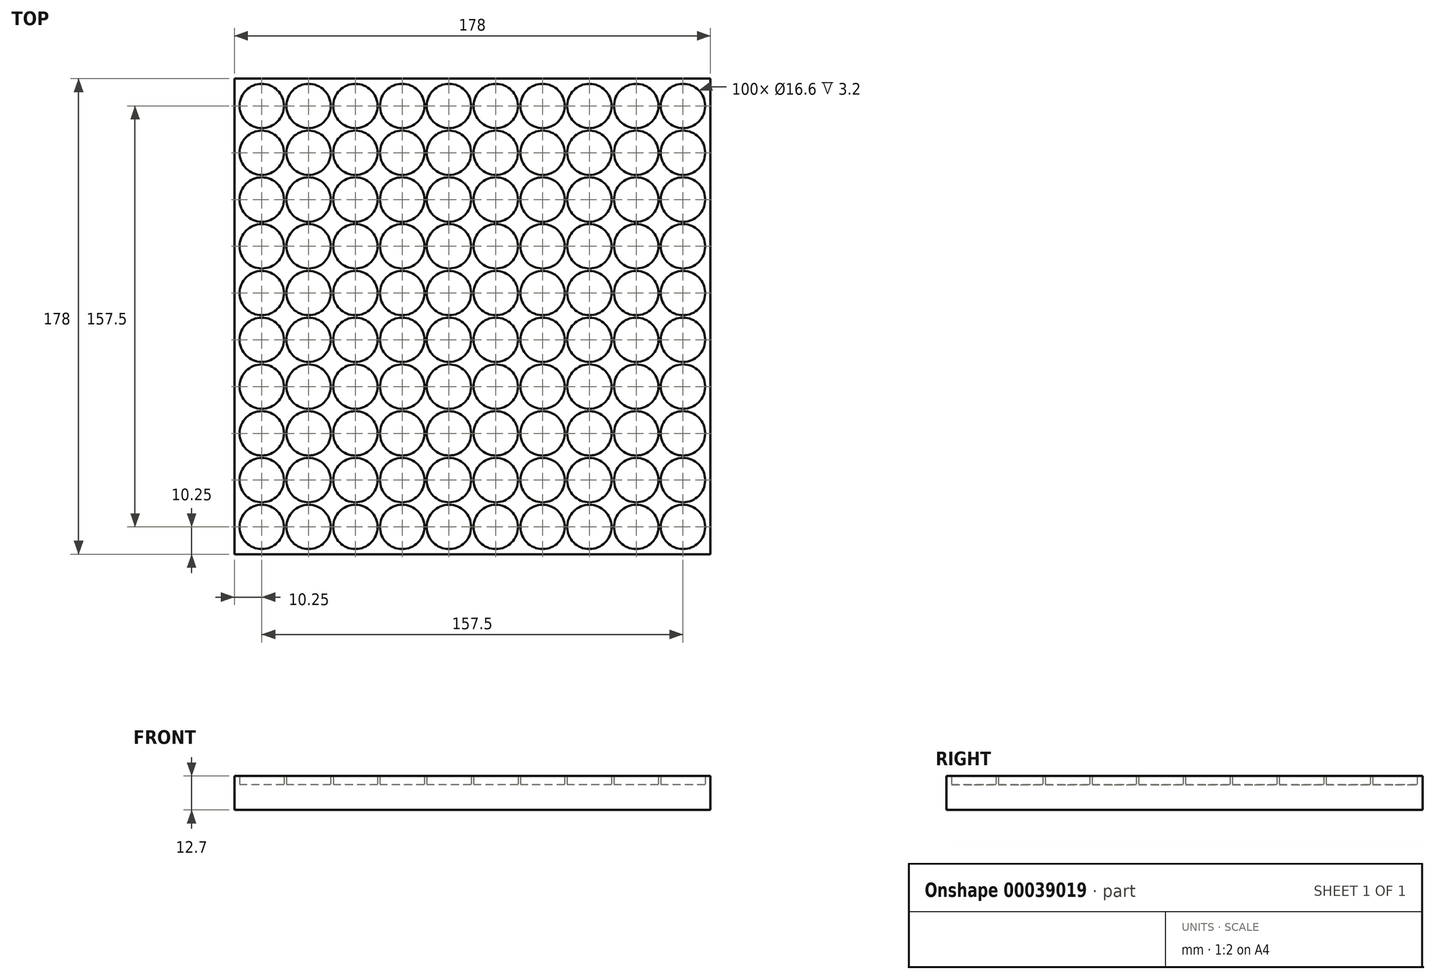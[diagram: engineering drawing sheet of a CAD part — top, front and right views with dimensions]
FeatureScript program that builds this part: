
annotation { "Feature Type Name" : "Feature", "Feature Type Description" : "" }
export const myFeature = defineFeature(function(context is Context, id is Id, definition is map)
    precondition{}
    {
        {
            var Q0;
            Q0=qCreatedBy(makeId("Top.planeOp"),FACE);
            var sketch = newSketch(context, id + "F0", { "sketchPlane" : qUnion([Q0])});
            skCircle(sketch, "E0", {"center": v(0, 0) * mm, "radius": 8.3 * mm});
            skCircle(sketch, "E1.0.1.0", {"center": v(0, 17.5) * mm, "radius": 8.3 * mm});
            skCircle(sketch, "E1.0.2.0", {"center": v(0, 35) * mm, "radius": 8.3 * mm});
            skCircle(sketch, "E1.0.3.0", {"center": v(0, 52.5) * mm, "radius": 8.3 * mm});
            skCircle(sketch, "E1.0.4.0", {"center": v(0, 70) * mm, "radius": 8.3 * mm});
            skCircle(sketch, "E1.0.5.0", {"center": v(0, 87.5) * mm, "radius": 8.3 * mm});
            skCircle(sketch, "E1.0.6.0", {"center": v(0, 105) * mm, "radius": 8.3 * mm});
            skCircle(sketch, "E1.0.7.0", {"center": v(0, 122.5) * mm, "radius": 8.3 * mm});
            skCircle(sketch, "E1.0.8.0", {"center": v(0, 140) * mm, "radius": 8.3 * mm});
            skCircle(sketch, "E1.0.9.0", {"center": v(0, 157.5) * mm, "radius": 8.3 * mm});
            skCircle(sketch, "E1.1.0.0", {"center": v(17.5, 0) * mm, "radius": 8.3 * mm});
            skCircle(sketch, "E1.1.1.0", {"center": v(17.5, 17.5) * mm, "radius": 8.3 * mm});
            skCircle(sketch, "E1.1.2.0", {"center": v(17.5, 35) * mm, "radius": 8.3 * mm});
            skCircle(sketch, "E1.1.3.0", {"center": v(17.5, 52.5) * mm, "radius": 8.3 * mm});
            skCircle(sketch, "E1.1.4.0", {"center": v(17.5, 70) * mm, "radius": 8.3 * mm});
            skCircle(sketch, "E1.1.5.0", {"center": v(17.5, 87.5) * mm, "radius": 8.3 * mm});
            skCircle(sketch, "E1.1.6.0", {"center": v(17.5, 105) * mm, "radius": 8.3 * mm});
            skCircle(sketch, "E1.1.7.0", {"center": v(17.5, 122.5) * mm, "radius": 8.3 * mm});
            skCircle(sketch, "E1.1.8.0", {"center": v(17.5, 140) * mm, "radius": 8.3 * mm});
            skCircle(sketch, "E1.1.9.0", {"center": v(17.5, 157.5) * mm, "radius": 8.3 * mm});
            skCircle(sketch, "E1.2.0.0", {"center": v(35, 0) * mm, "radius": 8.3 * mm});
            skCircle(sketch, "E1.2.1.0", {"center": v(35, 17.5) * mm, "radius": 8.3 * mm});
            skCircle(sketch, "E1.2.2.0", {"center": v(35, 35) * mm, "radius": 8.3 * mm});
            skCircle(sketch, "E1.2.3.0", {"center": v(35, 52.5) * mm, "radius": 8.3 * mm});
            skCircle(sketch, "E1.2.4.0", {"center": v(35, 70) * mm, "radius": 8.3 * mm});
            skCircle(sketch, "E1.2.5.0", {"center": v(35, 87.5) * mm, "radius": 8.3 * mm});
            skCircle(sketch, "E1.2.6.0", {"center": v(35, 105) * mm, "radius": 8.3 * mm});
            skCircle(sketch, "E1.2.7.0", {"center": v(35, 122.5) * mm, "radius": 8.3 * mm});
            skCircle(sketch, "E1.2.8.0", {"center": v(35, 140) * mm, "radius": 8.3 * mm});
            skCircle(sketch, "E1.2.9.0", {"center": v(35, 157.5) * mm, "radius": 8.3 * mm});
            skCircle(sketch, "E1.3.0.0", {"center": v(52.5, 0) * mm, "radius": 8.3 * mm});
            skCircle(sketch, "E1.3.1.0", {"center": v(52.5, 17.5) * mm, "radius": 8.3 * mm});
            skCircle(sketch, "E1.3.2.0", {"center": v(52.5, 35) * mm, "radius": 8.3 * mm});
            skCircle(sketch, "E1.3.3.0", {"center": v(52.5, 52.5) * mm, "radius": 8.3 * mm});
            skCircle(sketch, "E1.3.4.0", {"center": v(52.5, 70) * mm, "radius": 8.3 * mm});
            skCircle(sketch, "E1.3.5.0", {"center": v(52.5, 87.5) * mm, "radius": 8.3 * mm});
            skCircle(sketch, "E1.3.6.0", {"center": v(52.5, 105) * mm, "radius": 8.3 * mm});
            skCircle(sketch, "E1.3.7.0", {"center": v(52.5, 122.5) * mm, "radius": 8.3 * mm});
            skCircle(sketch, "E1.3.8.0", {"center": v(52.5, 140) * mm, "radius": 8.3 * mm});
            skCircle(sketch, "E1.3.9.0", {"center": v(52.5, 157.5) * mm, "radius": 8.3 * mm});
            skCircle(sketch, "E1.4.0.0", {"center": v(70, 0) * mm, "radius": 8.3 * mm});
            skCircle(sketch, "E1.4.1.0", {"center": v(70, 17.5) * mm, "radius": 8.3 * mm});
            skCircle(sketch, "E1.4.2.0", {"center": v(70, 35) * mm, "radius": 8.3 * mm});
            skCircle(sketch, "E1.4.3.0", {"center": v(70, 52.5) * mm, "radius": 8.3 * mm});
            skCircle(sketch, "E1.4.4.0", {"center": v(70, 70) * mm, "radius": 8.3 * mm});
            skCircle(sketch, "E1.4.5.0", {"center": v(70, 87.5) * mm, "radius": 8.3 * mm});
            skCircle(sketch, "E1.4.6.0", {"center": v(70, 105) * mm, "radius": 8.3 * mm});
            skCircle(sketch, "E1.4.7.0", {"center": v(70, 122.5) * mm, "radius": 8.3 * mm});
            skCircle(sketch, "E1.4.8.0", {"center": v(70, 140) * mm, "radius": 8.3 * mm});
            skCircle(sketch, "E1.4.9.0", {"center": v(70, 157.5) * mm, "radius": 8.3 * mm});
            skCircle(sketch, "E1.5.0.0", {"center": v(87.5, 0) * mm, "radius": 8.3 * mm});
            skCircle(sketch, "E1.5.1.0", {"center": v(87.5, 17.5) * mm, "radius": 8.3 * mm});
            skCircle(sketch, "E1.5.2.0", {"center": v(87.5, 35) * mm, "radius": 8.3 * mm});
            skCircle(sketch, "E1.5.3.0", {"center": v(87.5, 52.5) * mm, "radius": 8.3 * mm});
            skCircle(sketch, "E1.5.4.0", {"center": v(87.5, 70) * mm, "radius": 8.3 * mm});
            skCircle(sketch, "E1.5.5.0", {"center": v(87.5, 87.5) * mm, "radius": 8.3 * mm});
            skCircle(sketch, "E1.5.6.0", {"center": v(87.5, 105) * mm, "radius": 8.3 * mm});
            skCircle(sketch, "E1.5.7.0", {"center": v(87.5, 122.5) * mm, "radius": 8.3 * mm});
            skCircle(sketch, "E1.5.8.0", {"center": v(87.5, 140) * mm, "radius": 8.3 * mm});
            skCircle(sketch, "E1.5.9.0", {"center": v(87.5, 157.5) * mm, "radius": 8.3 * mm});
            skCircle(sketch, "E1.6.0.0", {"center": v(105, 0) * mm, "radius": 8.3 * mm});
            skCircle(sketch, "E1.6.1.0", {"center": v(105, 17.5) * mm, "radius": 8.3 * mm});
            skCircle(sketch, "E1.6.2.0", {"center": v(105, 35) * mm, "radius": 8.3 * mm});
            skCircle(sketch, "E1.6.3.0", {"center": v(105, 52.5) * mm, "radius": 8.3 * mm});
            skCircle(sketch, "E1.6.4.0", {"center": v(105, 70) * mm, "radius": 8.3 * mm});
            skCircle(sketch, "E1.6.5.0", {"center": v(105, 87.5) * mm, "radius": 8.3 * mm});
            skCircle(sketch, "E1.6.6.0", {"center": v(105, 105) * mm, "radius": 8.3 * mm});
            skCircle(sketch, "E1.6.7.0", {"center": v(105, 122.5) * mm, "radius": 8.3 * mm});
            skCircle(sketch, "E1.6.8.0", {"center": v(105, 140) * mm, "radius": 8.3 * mm});
            skCircle(sketch, "E1.6.9.0", {"center": v(105, 157.5) * mm, "radius": 8.3 * mm});
            skCircle(sketch, "E1.7.0.0", {"center": v(122.5, 0) * mm, "radius": 8.3 * mm});
            skCircle(sketch, "E1.7.1.0", {"center": v(122.5, 17.5) * mm, "radius": 8.3 * mm});
            skCircle(sketch, "E1.7.2.0", {"center": v(122.5, 35) * mm, "radius": 8.3 * mm});
            skCircle(sketch, "E1.7.3.0", {"center": v(122.5, 52.5) * mm, "radius": 8.3 * mm});
            skCircle(sketch, "E1.7.4.0", {"center": v(122.5, 70) * mm, "radius": 8.3 * mm});
            skCircle(sketch, "E1.7.5.0", {"center": v(122.5, 87.5) * mm, "radius": 8.3 * mm});
            skCircle(sketch, "E1.7.6.0", {"center": v(122.5, 105) * mm, "radius": 8.3 * mm});
            skCircle(sketch, "E1.7.7.0", {"center": v(122.5, 122.5) * mm, "radius": 8.3 * mm});
            skCircle(sketch, "E1.7.8.0", {"center": v(122.5, 140) * mm, "radius": 8.3 * mm});
            skCircle(sketch, "E1.7.9.0", {"center": v(122.5, 157.5) * mm, "radius": 8.3 * mm});
            skCircle(sketch, "E1.8.0.0", {"center": v(140, 0) * mm, "radius": 8.3 * mm});
            skCircle(sketch, "E1.8.1.0", {"center": v(140, 17.5) * mm, "radius": 8.3 * mm});
            skCircle(sketch, "E1.8.2.0", {"center": v(140, 35) * mm, "radius": 8.3 * mm});
            skCircle(sketch, "E1.8.3.0", {"center": v(140, 52.5) * mm, "radius": 8.3 * mm});
            skCircle(sketch, "E1.8.4.0", {"center": v(140, 70) * mm, "radius": 8.3 * mm});
            skCircle(sketch, "E1.8.5.0", {"center": v(140, 87.5) * mm, "radius": 8.3 * mm});
            skCircle(sketch, "E1.8.6.0", {"center": v(140, 105) * mm, "radius": 8.3 * mm});
            skCircle(sketch, "E1.8.7.0", {"center": v(140, 122.5) * mm, "radius": 8.3 * mm});
            skCircle(sketch, "E1.8.8.0", {"center": v(140, 140) * mm, "radius": 8.3 * mm});
            skCircle(sketch, "E1.8.9.0", {"center": v(140, 157.5) * mm, "radius": 8.3 * mm});
            skCircle(sketch, "E1.9.0.0", {"center": v(157.5, 0) * mm, "radius": 8.3 * mm});
            skCircle(sketch, "E1.9.1.0", {"center": v(157.5, 17.5) * mm, "radius": 8.3 * mm});
            skCircle(sketch, "E1.9.2.0", {"center": v(157.5, 35) * mm, "radius": 8.3 * mm});
            skCircle(sketch, "E1.9.3.0", {"center": v(157.5, 52.5) * mm, "radius": 8.3 * mm});
            skCircle(sketch, "E1.9.4.0", {"center": v(157.5, 70) * mm, "radius": 8.3 * mm});
            skCircle(sketch, "E1.9.5.0", {"center": v(157.5, 87.5) * mm, "radius": 8.3 * mm});
            skCircle(sketch, "E1.9.6.0", {"center": v(157.5, 105) * mm, "radius": 8.3 * mm});
            skCircle(sketch, "E1.9.7.0", {"center": v(157.5, 122.5) * mm, "radius": 8.3 * mm});
            skCircle(sketch, "E1.9.8.0", {"center": v(157.5, 140) * mm, "radius": 8.3 * mm});
            skCircle(sketch, "E1.9.9.0", {"center": v(157.5, 157.5) * mm, "radius": 8.3 * mm});
            skLineSegment(sketch, "E1.direction1", {"start": v(0, 0) * mm, "end": v(17.5, 0) * mm, "construction": true});
            skLineSegment(sketch, "E1.direction2", {"start": v(0, 0) * mm, "end": v(0, 17.5) * mm, "construction": true});
            skLineSegment(sketch, "E2", {"start": v(70, 87.5) * mm, "end": v(87.5, 70) * mm, "construction": true});
            skLineSegment(sketch, "E3", {"start": v(87.5, 87.5) * mm, "end": v(70, 70) * mm, "construction": true});
            skLineSegment(sketch, "E4.rect.bottom", {"start": v(167.75, -10.25) * mm, "end": v(-10.25, -10.25) * mm});
            skLineSegment(sketch, "E4.rect.top", {"start": v(167.75, 167.75) * mm, "end": v(-10.25, 167.75) * mm});
            skLineSegment(sketch, "E4.rect.left", {"start": v(167.75, -10.25) * mm, "end": v(167.75, 167.75) * mm});
            skLineSegment(sketch, "E4.rect.right", {"start": v(-10.25, -10.25) * mm, "end": v(-10.25, 167.75) * mm});
            skPoint(sketch, "E4.rect.middle", {"position": v(78.75, 78.75) * mm});
            skSolve(sketch);
        }
        {
            var Q0;
            Q0=makeQuery(id+"F0.imprint","IMPRINT",FACE,{"disambiguationData":[TD([[makeQuery(id+"F0.imprint","IMPRINT",EDGE,{"derivedFrom":sQuery(id+"F0.wireOp",EDGE,"E0")}),-1.0]])]});
            extrude(context, id + "F1", {"entities" : qUnion([Q0]), "depth" : 3.2 * mm});
        }
        {
            var Q0;
            Q0=qCreatedBy(makeId("Top.planeOp"),FACE);
            var sketch = newSketch(context, id + "F2", { "sketchPlane" : qUnion([Q0])});
            skLineSegment(sketch, "E5.0", {"start": v(167.75, -10.25) * mm, "end": v(-10.25, -10.25) * mm});
            skLineSegment(sketch, "E5.1", {"start": v(167.75, -10.25) * mm, "end": v(167.75, 167.75) * mm});
            skLineSegment(sketch, "E5.2", {"start": v(167.75, 167.75) * mm, "end": v(-10.25, 167.75) * mm});
            skLineSegment(sketch, "E5.3", {"start": v(-10.25, -10.25) * mm, "end": v(-10.25, 167.75) * mm});
            skSolve(sketch);
        }
        {
            var Q0;
            Q0 = qSketchRegion(id + "F2", true);
            extrude(context, id + "F3", {"entities" : qUnion([Q0]), "operationType" : NewBodyOperationType.ADD, "oppositeDirection" : true, "depth" : 9.5 * mm});
        }
    });
